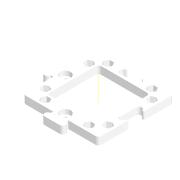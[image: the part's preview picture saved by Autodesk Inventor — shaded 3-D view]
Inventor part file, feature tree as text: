
AUTODESK INVENTOR PART (.ipt)
format: ipt  version: 2022 (Build 260153000, 153)  size: 476,160 bytes
history: native  units: mm
features: sketch x4, extrude x3, projected_geometry x3, mirror x2, other x1, pattern_circular x1, hole x1, chamfer x1, fillet x1
ambient origin geometry x8: Origin, YZ Plane, XZ Plane, XY Plane, X Axis, Y Axis, Z Axis, Center Point
bodies: Volumenkörper1 (feature_tree)
feature tree (17):
  extrude  "Extrusion1"  TaperAngle=0.0deg  [1 undecoded]
  mirror  "Mirror6"
  mirror  "Mirror7"
  extrude  "Extrusion13"  TaperAngle=0.0deg  [1 undecoded]
  extrude  "Extrusion14"  TaperAngle=0.0deg  [1 undecoded]
  other  "Work Axis4"
  pattern_circular  "Circular Pattern6"  [2 undecoded]
  hole  "Hole7"  [1 undecoded]
  chamfer  "Fase4"  [1 undecoded]
  fillet  "Rundung5"  [1 undecoded]
  sketch  "Skizze1"  dims[d5=0.0mm d6=0.0mm]
  sketch  "Sketch26"  dims[d7=0.0mm d8=0.0mm]
  projected_geometry  "Projected Loop21"
  sketch  "Sketch28"  dims[d9=0.0mm d13=0.0mm]
  sketch  "Sketch29"  dims[d14=0.0mm d20=0.0mm d21=0.0mm d22=0.0mm d23=0.0mm d24=0.0mm d25=3.0mm d26=0.0mm d27=0.0mm d28=0.0mm d29=0.0mm d30=0.0mm d31=0.0mm d32=0.0mm d33=0.0mm d34=0.0mm d46=0.0mm d47=0.0mm d48=0.0mm d49=-10.0mm d50=0.0mm d51=0.0mm d52=0.0mm d53=0.0mm d54=0.0mm d55=0.0mm d56=0.0mm d57=0.0mm d58=0.0mm d59=0.0mm d77=2.65mm d82=2.65mm d222=0.5mm d236=5.3mm d278=25.0mm d279=25.0mm d2=8.0mm d281=8.0mm d282=2.0mm d286=5.1mm d290=20.8mm d292=2.0mm d293=5.6mm d298=10.0mm d299=0.0mm d300=2.0mm d301=0.25mm d302=10.0mm d303=0.0mm d308=20.0mm d309=90.0deg d313=6.3mm d314=6.3mm d319=7.78mm d320=5.0mm d322=5.0mm d323=3.2mm d324=6.0mm d325=7.0mm d326=3.0mm d327=90.0deg d328=8.0mm d329=20.594885mm d331=0.0mm d332=0.0mm d360=0.5mm d361=2.0mm d362=45.0deg d365=7.0mm d367=7.0mm d369=4.2mm d370=0.0mm d380=45.0deg d384=0.75mm d385=5.0mm d386=5.0mm d387=2.0mm d388=0.25mm d391=0.1mm d392=5.05mm d393=5.05mm d394=1.96mm d396=5.45mm d397=7.05mm]
  projected_geometry  "Projected Loop24"
  projected_geometry  "Projizierte Kontur27"
note: 8 required parameter values undecoded (feature->parameter linkage not recoverable at this tier; creation-order binding heuristic only, values carry confidence <= 0.55)
